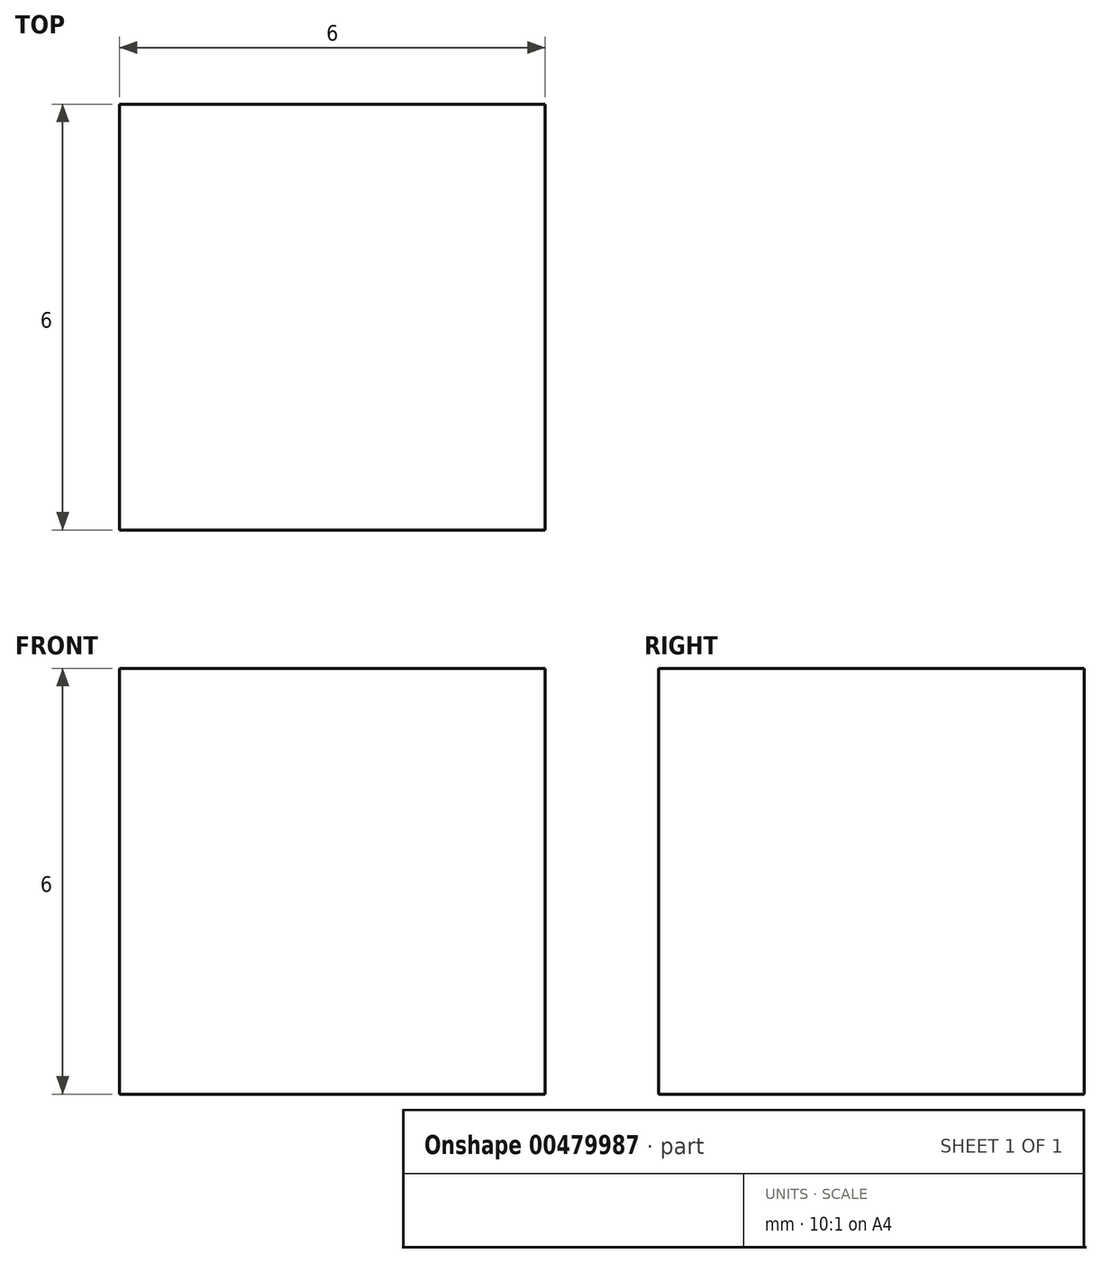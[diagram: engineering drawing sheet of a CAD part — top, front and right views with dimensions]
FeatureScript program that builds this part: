
annotation { "Feature Type Name" : "Feature", "Feature Type Description" : "" }
export const myFeature = defineFeature(function(context is Context, id is Id, definition is map)
    precondition{}
    {
        {
            var Q0;
            Q0=qCreatedBy(makeId("Front.planeOp"),FACE);
            var sketch = newSketch(context, id + "F0", { "sketchPlane" : qUnion([Q0])});
            skLineSegment(sketch, "E0.bottom", {"start": v(3, -3) * mm, "end": v(-3, -3) * mm});
            skLineSegment(sketch, "E0.top", {"start": v(3, 3) * mm, "end": v(-3, 3) * mm});
            skLineSegment(sketch, "E0.left", {"start": v(3, -3) * mm, "end": v(3, 3) * mm});
            skLineSegment(sketch, "E0.right", {"start": v(-3, -3) * mm, "end": v(-3, 3) * mm});
            skPoint(sketch, "E0.middle", {"position": v(0, 0) * mm});
            skSolve(sketch);
        }
        {
            var Q0;
            Q0=makeQuery(id+"F0.imprint","IMPRINT",FACE,{"disambiguationData":[TD([[makeQuery(id+"F0.imprint","IMPRINT",EDGE,{"derivedFrom":sQuery(id+"F0.wireOp",EDGE,"E0.bottom")}),-1.0]])]});
            extrude(context, id + "F1", {"entities" : qUnion([Q0]), "depth" : 6 * mm});
        }
    });
